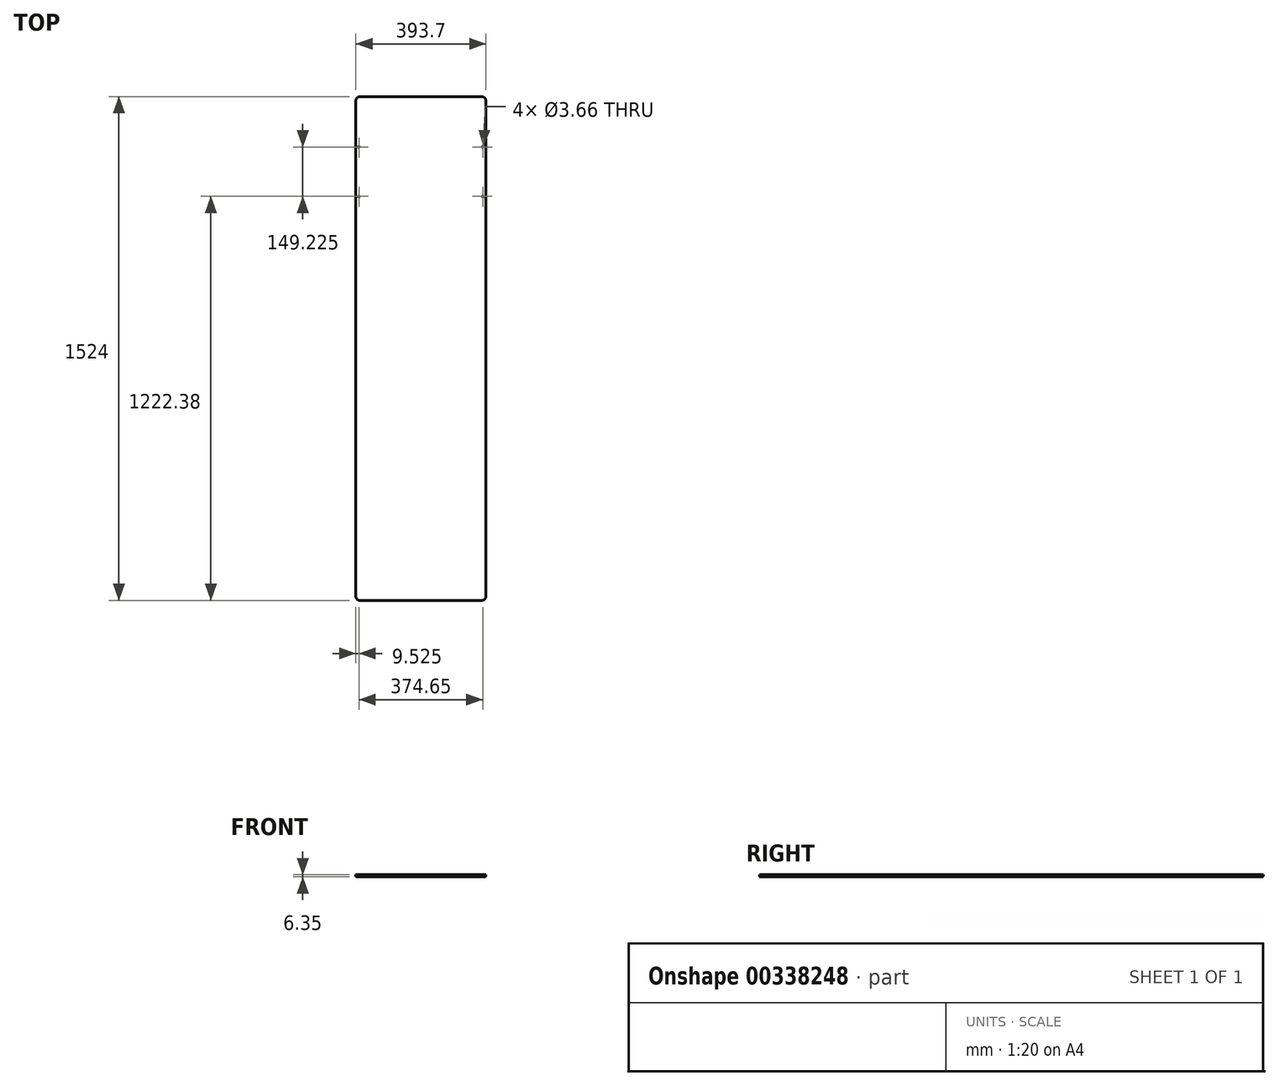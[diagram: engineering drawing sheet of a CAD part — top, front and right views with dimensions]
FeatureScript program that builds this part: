
annotation { "Feature Type Name" : "Feature", "Feature Type Description" : "" }
export const myFeature = defineFeature(function(context is Context, id is Id, definition is map)
    precondition{}
    {
        {
            var Q0;
            Q0=qCreatedBy(makeId("Top.planeOp"),FACE);
            var sketch = newSketch(context, id + "F0", { "sketchPlane" : qUnion([Q0])});
            skLineSegment(sketch, "E0.bottom", {"start": v(0, 0) * mm, "end": v(393.7, 0) * mm});
            skLineSegment(sketch, "E0.top", {"start": v(0, -1524) * mm, "end": v(393.7, -1524) * mm});
            skLineSegment(sketch, "E0.left", {"start": v(0, 0) * mm, "end": v(0, -1524) * mm});
            skLineSegment(sketch, "E0.right", {"start": v(393.7, 0) * mm, "end": v(393.7, -1524) * mm});
            skLineSegment(sketch, "E1", {"start": v(384.18, 0) * mm, "end": v(384.18, -152.4) * mm, "construction": true});
            skLineSegment(sketch, "E2", {"start": v(384.18, -152.4) * mm, "end": v(384.18, -301.63) * mm, "construction": true});
            skLineSegment(sketch, "E3", {"start": v(9.52, 0) * mm, "end": v(9.52, -152.4) * mm, "construction": true});
            skLineSegment(sketch, "E4", {"start": v(9.52, -152.4) * mm, "end": v(9.53, -301.63) * mm, "construction": true});
            skLineSegment(sketch, "E5", {"start": v(384.18, -152.4) * mm, "end": v(393.7, -152.4) * mm, "construction": true});
            skLineSegment(sketch, "E6", {"start": v(9.52, -152.4) * mm, "end": v(0, -152.4) * mm, "construction": true});
            skCircle(sketch, "E7", {"center": v(9.52, -152.4) * mm, "radius": 1.83 * mm});
            skCircle(sketch, "E8", {"center": v(9.53, -301.63) * mm, "radius": 1.83 * mm});
            skCircle(sketch, "E9", {"center": v(384.18, -301.63) * mm, "radius": 1.83 * mm});
            skCircle(sketch, "E10", {"center": v(384.18, -152.4) * mm, "radius": 1.83 * mm});
            skSolve(sketch);
        }
        {
            var Q0;
            Q0 = qSketchRegion(id + "F0", true);
            extrude(context, id + "F1", {"entities" : qUnion([Q0]), "depth" : 6.35 * mm});
        }
        {
            var Q0;
            Q0=makeQuery(id+"F1.opExtrude","SWEPT_EDGE",EDGE,{"disambiguationData":[OSD([sQuery(id+"F0.wireOp",EDGE,"E0.top"),sQuery(id+"F0.wireOp",EDGE,"E0.right")])]});
            var Q1;
            Q1=makeQuery(id+"F1.opExtrude","SWEPT_EDGE",EDGE,{"disambiguationData":[OSD([sQuery(id+"F0.wireOp",EDGE,"E0.top"),sQuery(id+"F0.wireOp",EDGE,"E0.left")])]});
            var Q2;
            Q2=makeQuery(id+"F1.opExtrude","SWEPT_EDGE",EDGE,{"disambiguationData":[OSD([sQuery(id+"F0.wireOp",EDGE,"E0.bottom"),sQuery(id+"F0.wireOp",EDGE,"E0.right")])]});
            var Q3;
            Q3=makeQuery(id+"F1.opExtrude","SWEPT_EDGE",EDGE,{"disambiguationData":[OSD([sQuery(id+"F0.wireOp",EDGE,"E0.bottom"),sQuery(id+"F0.wireOp",EDGE,"E0.left")])]});
            fillet(context, id + "F2", {"entities" : qUnion([Q0, Q1, Q2, Q3]), "radius" : 12.7 * mm, "tangentPropagation" : true, "allowEdgeOverflow" : false});
        }
        {
            var Q0;
            Q0=makeQuery(id+"F1.opExtrude","CAP_EDGE",EDGE,{"disambiguationData":[OSD([sQuery(id+"F0.wireOp",EDGE,"E0.bottom")])],"isStart":true});
            fillet(context, id + "F3", {"entities" : qUnion([Q0]), "radius" : 3.17 * mm, "tangentPropagation" : true, "allowEdgeOverflow" : false});
        }
    });
